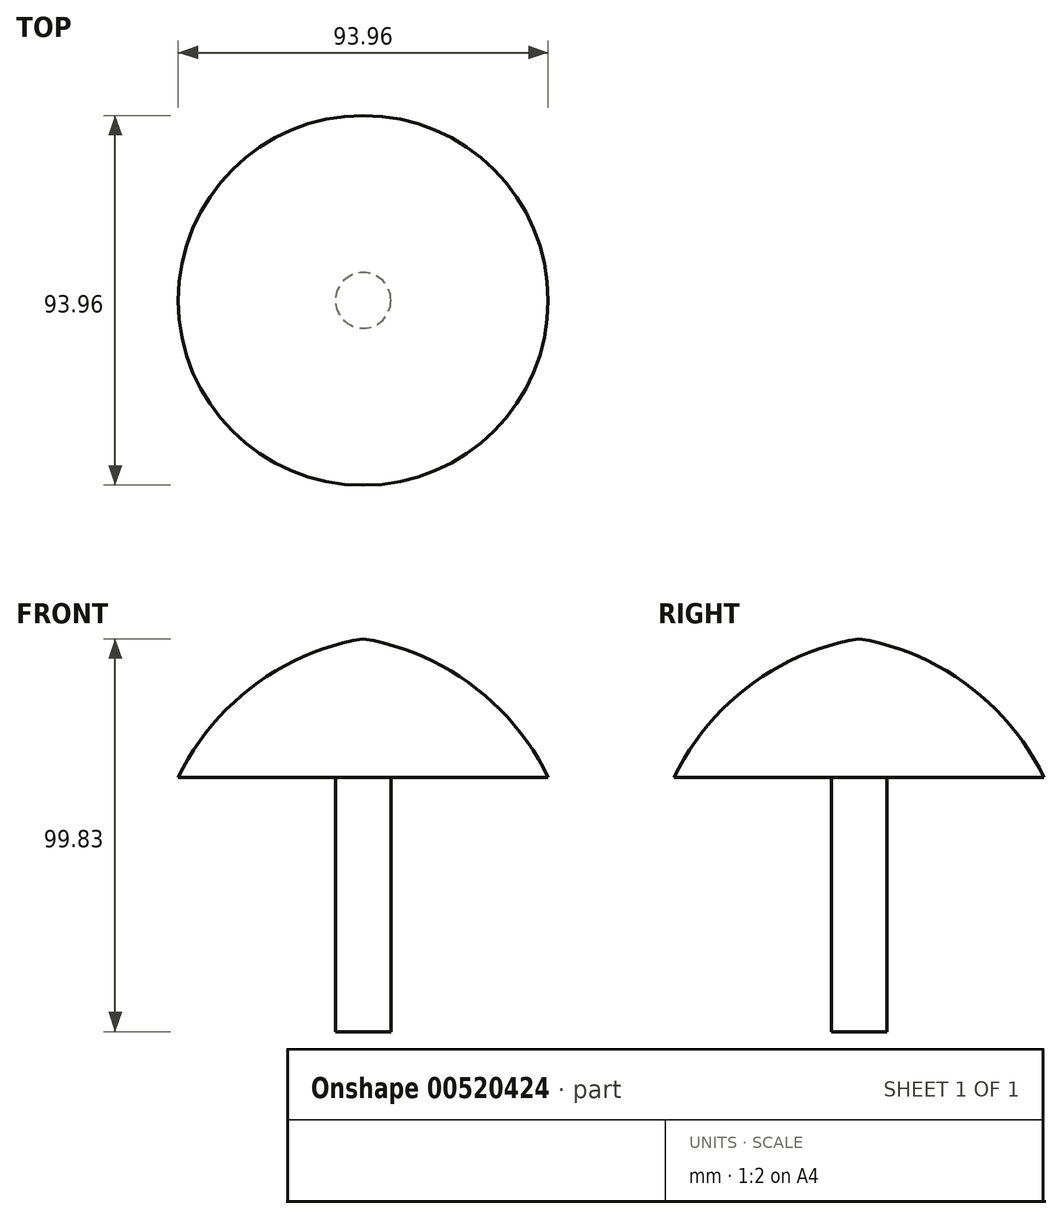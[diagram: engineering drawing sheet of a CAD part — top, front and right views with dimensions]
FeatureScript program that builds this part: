
annotation { "Feature Type Name" : "Feature", "Feature Type Description" : "" }
export const myFeature = defineFeature(function(context is Context, id is Id, definition is map)
    precondition{}
    {
        {
            var Q0;
            Q0=qCreatedBy(makeId("Front.planeOp"),FACE);
            var sketch = newSketch(context, id + "F0", { "sketchPlane" : qUnion([Q0])});
            skLineSegment(sketch, "E0", {"start": v(0, 79.42) * mm, "end": v(0, -77.37) * mm, "construction": true});
            skArc(sketch, "E1", {"start": v(46.98, 20.7) * mm, "mid": v(27.78, 44.03) * mm, "end": v(0, 55.93) * mm});
            skLineSegment(sketch, "E2", {"start": v(46.98, 20.7) * mm, "end": v(7.05, 20.7) * mm});
            skLineSegment(sketch, "E3", {"start": v(7.05, 20.7) * mm, "end": v(7.05, -43.9) * mm});
            skLineSegment(sketch, "E4", {"start": v(7.05, -43.9) * mm, "end": v(0, -43.9) * mm});
            skLineSegment(sketch, "E5", {"start": v(0, -43.9) * mm, "end": v(0, 20.7) * mm, "construction": true});
            skLineSegment(sketch, "E6", {"start": v(0, 55.93) * mm, "end": v(0, -43.9) * mm});
            skSolve(sketch);
        }
        {
            var Q0;
            Q0=makeQuery(id+"F0.imprint","IMPRINT",FACE,{"disambiguationData":[TD([[makeQuery(id+"F0.imprint","IMPRINT",EDGE,{"derivedFrom":sQuery(id+"F0.wireOp",EDGE,"E1")}),1.0]])]});
            var Q1;
            Q1=sQuery(id+"F0.wireOp",EDGE,"E6");
            revolve(context, id + "F1", {"entities" : qUnion([Q0]), "axis" : qUnion([Q1]), "revolveType" : RevolveType.FULL});
        }
    });
